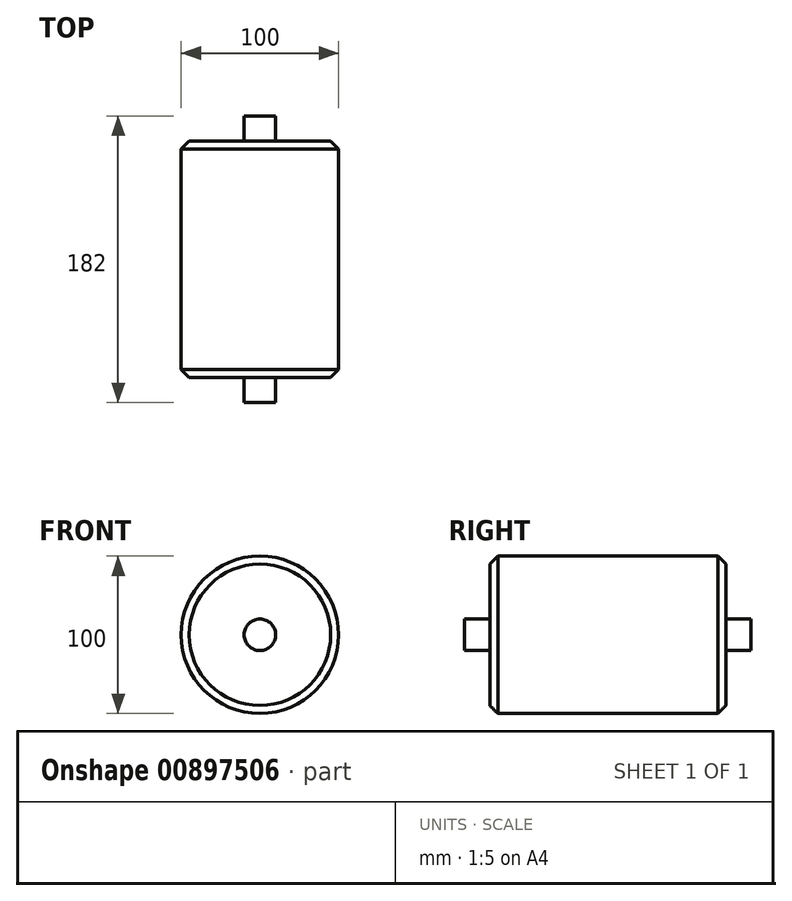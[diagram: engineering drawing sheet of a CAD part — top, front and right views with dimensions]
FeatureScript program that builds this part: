
annotation { "Feature Type Name" : "Feature", "Feature Type Description" : "" }
export const myFeature = defineFeature(function(context is Context, id is Id, definition is map)
    precondition{}
    {
        {
            var Q0;
            Q0=qCreatedBy(makeId("Front.planeOp"),FACE);
            var sketch = newSketch(context, id + "F0", { "sketchPlane" : qUnion([Q0])});
            skCircle(sketch, "E0", {"center": v(0, 0) * mm, "radius": 50 * mm});
            skSolve(sketch);
        }
        {
            var Q0;
            Q0=makeQuery(id+"F0.imprint","IMPRINT",FACE,{"disambiguationData":[TD([[makeQuery(id+"F0.imprint","IMPRINT",EDGE,{"derivedFrom":sQuery(id+"F0.wireOp",EDGE,"E0")}),1.0]])]});
            extrude(context, id + "F1", {"entities" : qUnion([Q0]), "depth" : 75 * mm, "offsetDistance" : 25.4 * mm});
        }
        {
            var Q0;
            Q0=makeQuery(id+"F1.opExtrude","CAP_FACE",FACE,{"disambiguationData":[OSD([sQuery(id+"F0.wireOp",EDGE,"E0")])],"isStart":true});
            extrude(context, id + "F2", {"entities" : qUnion([Q0]), "operationType" : NewBodyOperationType.ADD, "depth" : 75 * mm, "offsetDistance" : 25.4 * mm});
        }
        {
            var Q0;
            Q0=makeQuery(id+"F1.opExtrude","CAP_FACE",FACE,{"disambiguationData":[OSD([sQuery(id+"F0.wireOp",EDGE,"E0")])],"isStart":false});
            var sketch = newSketch(context, id + "F3", { "sketchPlane" : qUnion([Q0])});
            skCircle(sketch, "E1", {"center": v(0, 0) * mm, "radius": 10 * mm});
            skSolve(sketch);
        }
        {
            var Q0;
            Q0=makeQuery(id+"F3.imprint","IMPRINT",FACE,{"disambiguationData":[TD([[makeQuery(id+"F3.imprint","IMPRINT",EDGE,{"derivedFrom":sQuery(id+"F3.wireOp",EDGE,"E1")}),1.0]])]});
            extrude(context, id + "F4", {"entities" : qUnion([Q0]), "operationType" : NewBodyOperationType.ADD, "depth" : 16 * mm, "offsetDistance" : 25.4 * mm});
        }
        {
            var Q0;
            Q0=makeQuery(id+"F2.opExtrude","CAP_FACE",FACE,{"disambiguationData":[OSD([sQuery(id+"F0.wireOp",EDGE,"E0")])],"isStart":false});
            var sketch = newSketch(context, id + "F5", { "sketchPlane" : qUnion([Q0])});
            skCircle(sketch, "E2", {"center": v(0, 0) * mm, "radius": 10 * mm});
            skSolve(sketch);
        }
        {
            var Q0;
            Q0=makeQuery(id+"F5.imprint","IMPRINT",FACE,{"disambiguationData":[TD([[makeQuery(id+"F5.imprint","IMPRINT",EDGE,{"derivedFrom":sQuery(id+"F5.wireOp",EDGE,"E2")}),1.0]])]});
            extrude(context, id + "F6", {"entities" : qUnion([Q0]), "operationType" : NewBodyOperationType.ADD, "depth" : 16 * mm, "offsetDistance" : 25.4 * mm});
        }
        {
            var Q0;
            Q0=makeQuery(id+"F1.opExtrude","CAP_EDGE",EDGE,{"disambiguationData":[OSD([sQuery(id+"F0.wireOp",EDGE,"E0")])],"isStart":false});
            chamfer(context, id + "F7", {"entities" : qUnion([Q0]), "width" : 5.08 * mm, "tangentPropagation" : true});
        }
        {
            var Q0;
            Q0=makeQuery(id+"F2.opExtrude","CAP_EDGE",EDGE,{"disambiguationData":[OSD([sQuery(id+"F0.wireOp",EDGE,"E0")])],"isStart":false});
            chamfer(context, id + "F8", {"entities" : qUnion([Q0]), "width" : 5.08 * mm, "tangentPropagation" : true});
        }
    });
